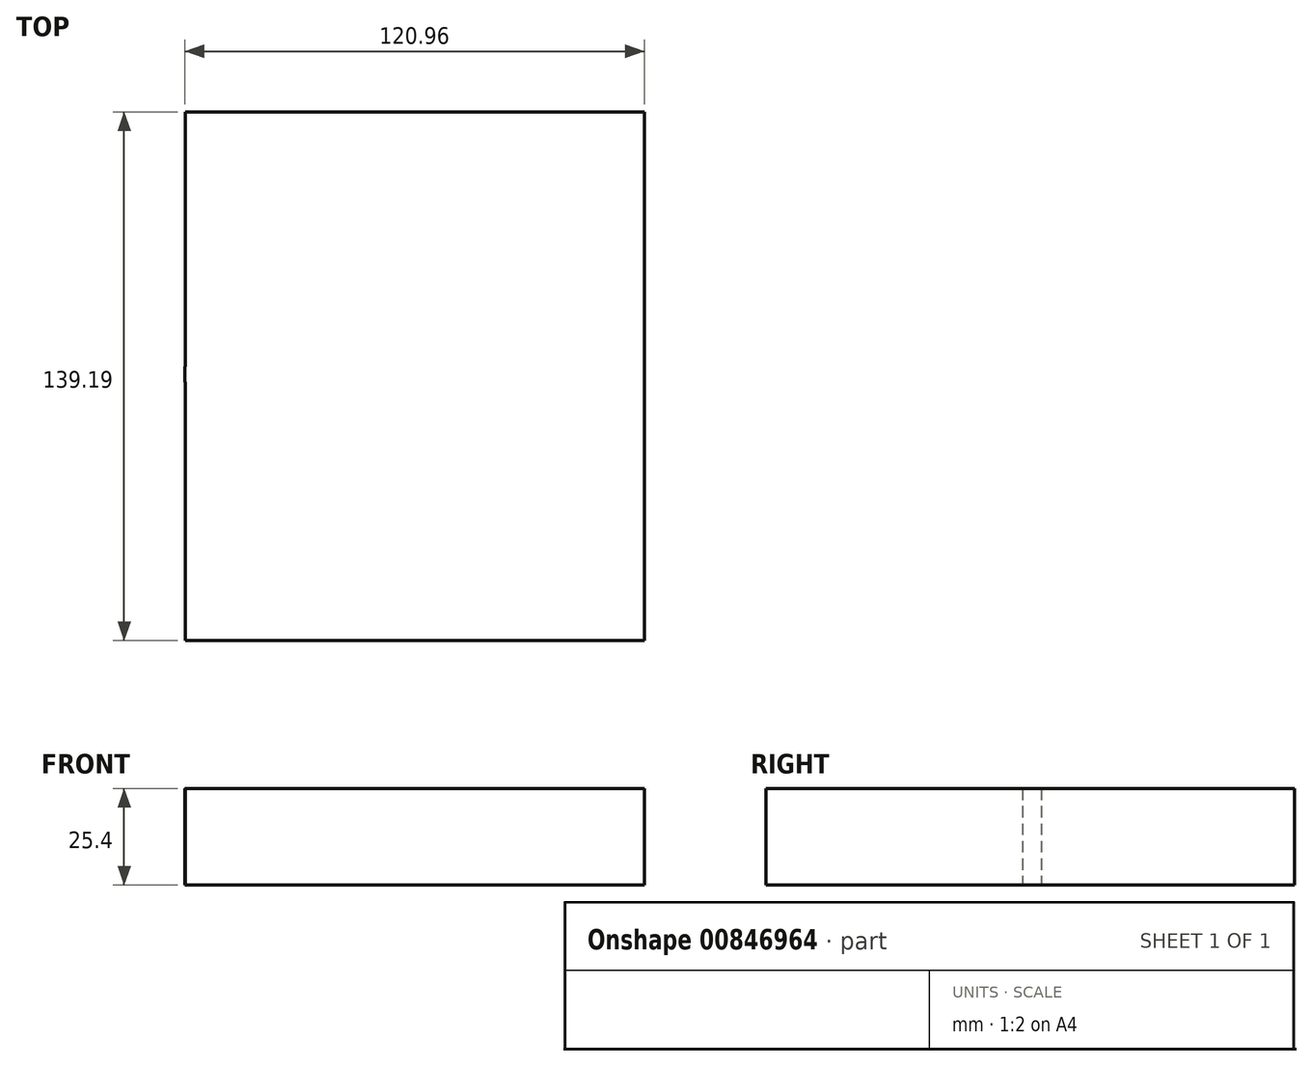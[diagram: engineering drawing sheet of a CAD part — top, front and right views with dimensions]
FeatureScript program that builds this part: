
annotation { "Feature Type Name" : "Feature", "Feature Type Description" : "" }
export const myFeature = defineFeature(function(context is Context, id is Id, definition is map)
    precondition{}
    {
        {
            var Q0;
            Q0=qCreatedBy(makeId("Top.planeOp"),FACE);
            var sketch = newSketch(context, id + "F0", { "sketchPlane" : qUnion([Q0])});
            skLineSegment(sketch, "E0.bottom", {"start": v(-58.27, 69.08) * mm, "end": v(62.64, 69.08) * mm});
            skLineSegment(sketch, "E0.top", {"start": v(-58.27, -70.1) * mm, "end": v(62.64, -70.1) * mm});
            skLineSegment(sketch, "E0.left", {"start": v(-58.27, 69.08) * mm, "end": v(-58.27, -70.1) * mm});
            skLineSegment(sketch, "E0.right", {"start": v(62.64, 69.08) * mm, "end": v(62.64, -70.1) * mm});
            skCircle(sketch, "E1", {"center": v(0, 0) * mm, "radius": 58.32 * mm});
            skCircle(sketch, "E2", {"center": v(0, 0) * mm, "radius": 50.91 * mm});
            skCircle(sketch, "E3", {"center": v(0, 0) * mm, "radius": 45.33 * mm});
            skCircle(sketch, "E4", {"center": v(0, 0) * mm, "radius": 38.3 * mm});
            skCircle(sketch, "E5", {"center": v(0, 0) * mm, "radius": 31.44 * mm});
            skCircle(sketch, "E6", {"center": v(0, 0) * mm, "radius": 25.8 * mm});
            skCircle(sketch, "E7", {"center": v(0, 0) * mm, "radius": 20.89 * mm});
            skCircle(sketch, "E8", {"center": v(0, 0) * mm, "radius": 16.4 * mm});
            skCircle(sketch, "E9", {"center": v(0, 0) * mm, "radius": 11.96 * mm});
            skCircle(sketch, "E10", {"center": v(0, 0) * mm, "radius": 10.1 * mm});
            skCircle(sketch, "E11", {"center": v(0, 0) * mm, "radius": 7.43 * mm});
            skCircle(sketch, "E12", {"center": v(0, 0) * mm, "radius": 5.24 * mm});
            skCircle(sketch, "E13", {"center": v(0, 0) * mm, "radius": 3.4 * mm});
            skSolve(sketch);
        }
        {
            var Q0;
            {var subQ4=sQuery(id+"F0.wireOp",EDGE,"E0.bottom");Q0=makeQuery(id+"F0.imprint","IMPRINT",FACE,{"disambiguationData":[TD([[makeQuery(id+"F0.imprint","IMPRINT",EDGE,{"derivedFrom":subQ4}),-1.0]])]});}
            var Q1;
            Q1=makeQuery(id+"F0.imprint","IMPRINT",FACE,{"disambiguationData":[TD([[makeQuery(id+"F0.imprint","IMPRINT",EDGE,{"derivedFrom":sQuery(id+"F0.wireOp",EDGE,"E8")}),1.0]])]});
            var Q2;
            Q2=makeQuery(id+"F0.imprint","IMPRINT",FACE,{"disambiguationData":[TD([[makeQuery(id+"F0.imprint","IMPRINT",EDGE,{"derivedFrom":sQuery(id+"F0.wireOp",EDGE,"E7")}),1.0]])]});
            var Q3;
            Q3=makeQuery(id+"F0.imprint","IMPRINT",FACE,{"disambiguationData":[TD([[makeQuery(id+"F0.imprint","IMPRINT",EDGE,{"derivedFrom":sQuery(id+"F0.wireOp",EDGE,"E5")}),1.0]])]});
            var Q4;
            Q4=makeQuery(id+"F0.imprint","IMPRINT",FACE,{"disambiguationData":[TD([[makeQuery(id+"F0.imprint","IMPRINT",EDGE,{"derivedFrom":sQuery(id+"F0.wireOp",EDGE,"E10")}),1.0]])]});
            var Q5;
            Q5=makeQuery(id+"F0.imprint","IMPRINT",FACE,{"disambiguationData":[TD([[makeQuery(id+"F0.imprint","IMPRINT",EDGE,{"derivedFrom":sQuery(id+"F0.wireOp",EDGE,"E11")}),1.0]])]});
            var Q6;
            Q6=makeQuery(id+"F0.imprint","IMPRINT",FACE,{"disambiguationData":[TD([[makeQuery(id+"F0.imprint","IMPRINT",EDGE,{"derivedFrom":sQuery(id+"F0.wireOp",EDGE,"E9")}),1.0]])]});
            var Q7;
            Q7=makeQuery(id+"F0.imprint","IMPRINT",FACE,{"disambiguationData":[TD([[makeQuery(id+"F0.imprint","IMPRINT",EDGE,{"derivedFrom":sQuery(id+"F0.wireOp",EDGE,"E6")}),1.0]])]});
            var Q8;
            Q8=makeQuery(id+"F0.imprint","IMPRINT",FACE,{"disambiguationData":[TD([[makeQuery(id+"F0.imprint","IMPRINT",EDGE,{"derivedFrom":sQuery(id+"F0.wireOp",EDGE,"E13")}),1.0]])]});
            var Q9;
            Q9=makeQuery(id+"F0.imprint","IMPRINT",FACE,{"disambiguationData":[TD([[makeQuery(id+"F0.imprint","IMPRINT",EDGE,{"derivedFrom":sQuery(id+"F0.wireOp",EDGE,"E12")}),1.0]])]});
            var Q10;
            Q10=makeQuery(id+"F0.imprint","IMPRINT",FACE,{"disambiguationData":[TD([[makeQuery(id+"F0.imprint","IMPRINT",EDGE,{"derivedFrom":sQuery(id+"F0.wireOp",EDGE,"E4")}),1.0]])]});
            var Q11;
            Q11=makeQuery(id+"F0.imprint","IMPRINT",FACE,{"disambiguationData":[TD([[makeQuery(id+"F0.imprint","IMPRINT",EDGE,{"derivedFrom":sQuery(id+"F0.wireOp",EDGE,"E2")}),-1.0]])]});
            var Q12;
            Q12=makeQuery(id+"F0.imprint","IMPRINT",FACE,{"disambiguationData":[TD([[makeQuery(id+"F0.imprint","IMPRINT",EDGE,{"derivedFrom":sQuery(id+"F0.wireOp",EDGE,"E3")}),1.0]])]});
            var Q13;
            Q13=makeQuery(id+"F0.imprint","IMPRINT",FACE,{"disambiguationData":[TD([[makeQuery(id+"F0.imprint","IMPRINT",EDGE,{"derivedFrom":sQuery(id+"F0.wireOp",EDGE,"E2")}),1.0]])]});
            var Q14;
            {var subQ0=sQuery(id+"F0.wireOp",EDGE,"E1");var subQ1=sQuery(id+"F0.wireOp",EDGE,"E0.left");var subQ2=makeQuery(id+"F0.imprint","INTERSECT",VERTEX,{"disambiguationData":[OD(0.0)],"derivedFrom":[subQ1,subQ0]});Q14=makeQuery(id+"F0.imprint","IMPRINT",FACE,{"disambiguationData":[TD([[makeQuery(id+"F0.imprint","IMPRINT",EDGE,{"disambiguationData":[TD([[subQ2,-1.0]])],"derivedFrom":subQ1}),-1.0]])]});}
            extrude(context, id + "F1", {"entities" : qUnion([Q0, Q1, Q2, Q3, Q4, Q5, Q6, Q7, Q8, Q9, Q10, Q11, Q12, Q13, Q14]), "depth" : 25.4 * mm, "offsetDistance" : 25.4 * mm});
        }
    });
